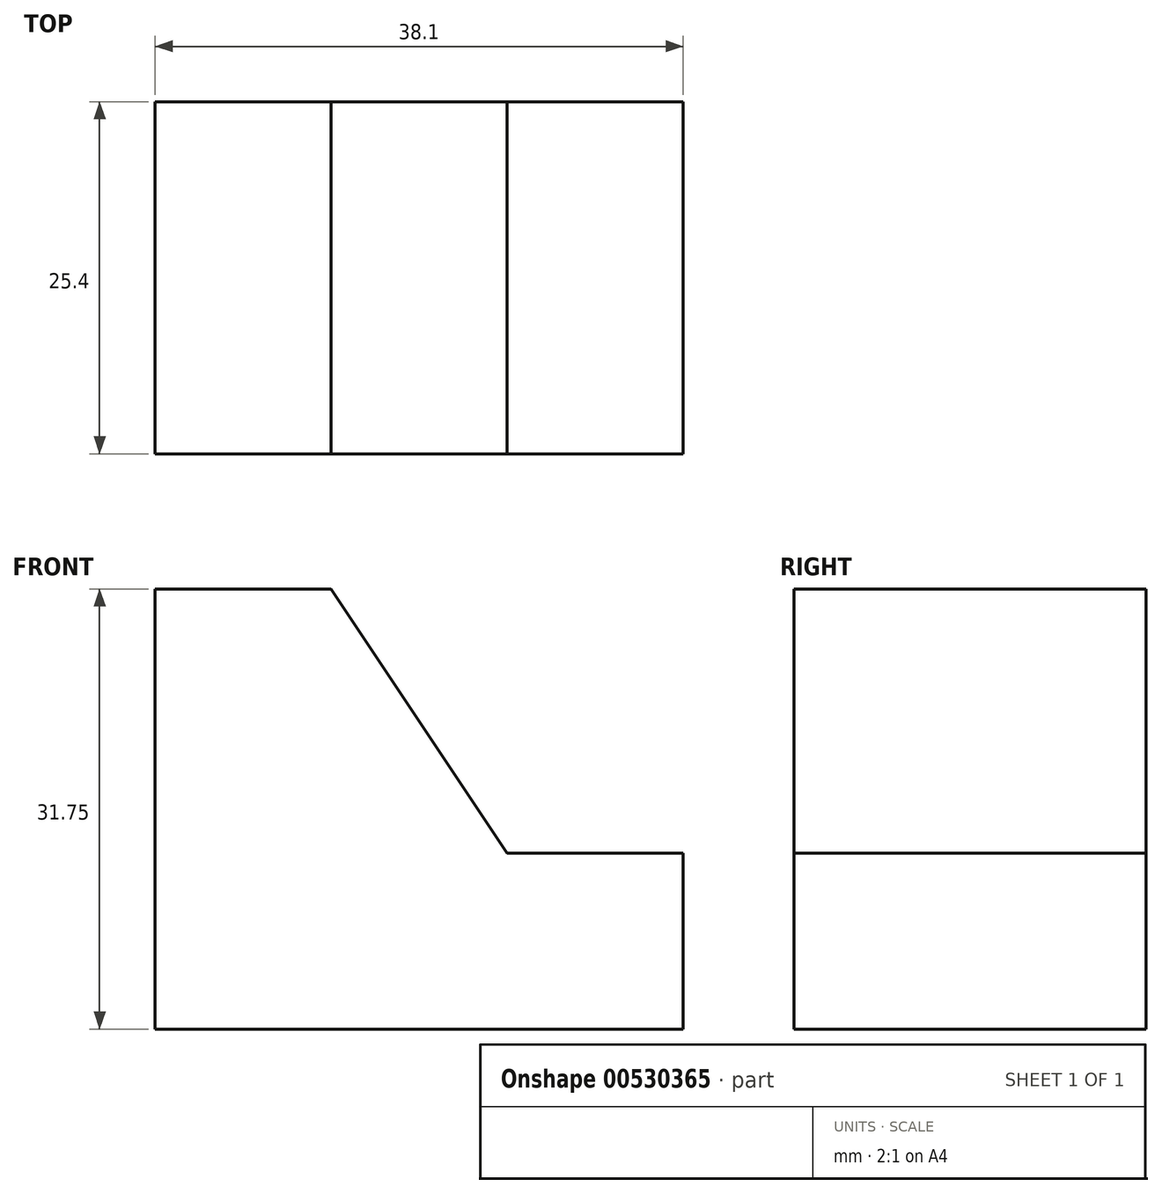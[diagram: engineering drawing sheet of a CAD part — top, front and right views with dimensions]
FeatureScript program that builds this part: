
annotation { "Feature Type Name" : "Feature", "Feature Type Description" : "" }
export const myFeature = defineFeature(function(context is Context, id is Id, definition is map)
    precondition{}
    {
        {
            var Q0;
            Q0=qCreatedBy(makeId("Front.planeOp"),FACE);
            var sketch = newSketch(context, id + "F0", { "sketchPlane" : qUnion([Q0])});
            skLineSegment(sketch, "E0", {"start": v(-38.1, 0) * mm, "end": v(0, 0) * mm});
            skLineSegment(sketch, "E1", {"start": v(0, 0) * mm, "end": v(0, 12.7) * mm});
            skLineSegment(sketch, "E2", {"start": v(0, 12.7) * mm, "end": v(-12.7, 12.7) * mm});
            skLineSegment(sketch, "E3", {"start": v(-12.7, 12.7) * mm, "end": v(-25.4, 31.75) * mm});
            skLineSegment(sketch, "E4", {"start": v(-25.4, 31.75) * mm, "end": v(-38.1, 31.75) * mm});
            skLineSegment(sketch, "E5", {"start": v(-38.1, 31.75) * mm, "end": v(-38.1, 0) * mm});
            skSolve(sketch);
        }
        {
            var Q0;
            Q0=makeQuery(id+"F0.imprint","IMPRINT",FACE,{"disambiguationData":[TD([[makeQuery(id+"F0.imprint","IMPRINT",EDGE,{"derivedFrom":sQuery(id+"F0.wireOp",EDGE,"E0")}),1.0]])]});
            extrude(context, id + "F1", {"entities" : qUnion([Q0]), "depth" : 25.4 * mm, "offsetDistance" : 25.4 * mm});
        }
    });
